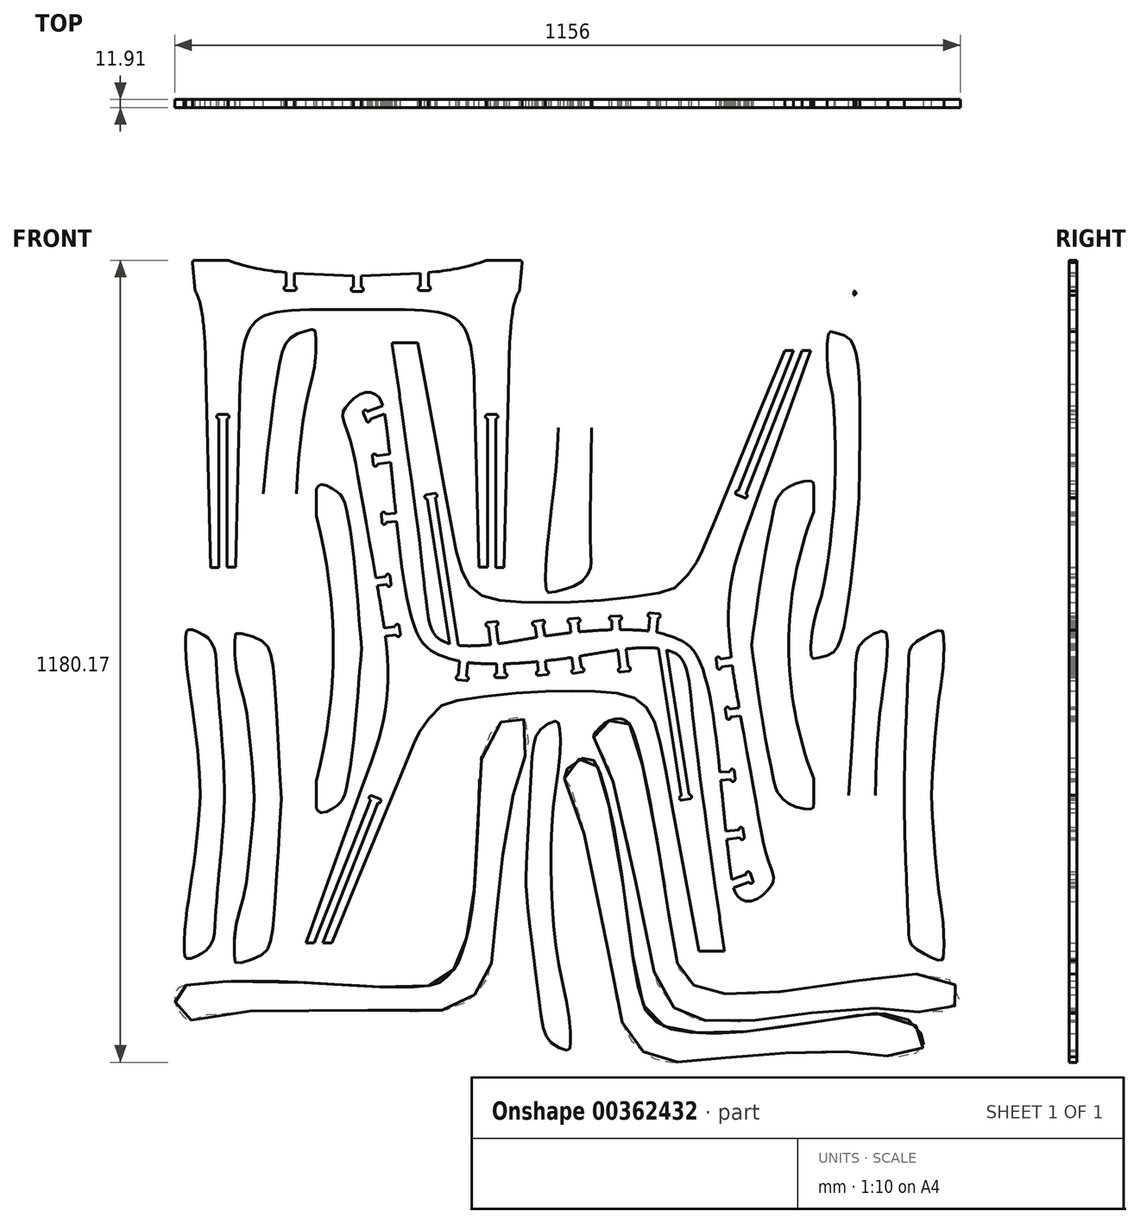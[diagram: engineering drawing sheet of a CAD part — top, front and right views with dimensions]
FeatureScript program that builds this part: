
annotation { "Feature Type Name" : "Feature", "Feature Type Description" : "" }
export const myFeature = defineFeature(function(context is Context, id is Id, definition is map)
    precondition{}
    {
        {
            var Q0;
            Q0=qCreatedBy(makeId("Front.planeOp"),FACE);
            var sketch = newSketch(context, id + "F0", { "sketchPlane" : qUnion([Q0])});
            skLineSegment(sketch, "E0", {"start": v(-81.62, 205.23) * mm, "end": v(-81.62, 184.98) * mm});
            skLineSegment(sketch, "E1", {"start": v(-81.62, 184.98) * mm, "end": v(-81.62, 178.63) * mm});
            skLineSegment(sketch, "E2", {"start": v(-81.62, 178.63) * mm, "end": v(-69.72, 178.63) * mm});
            skLineSegment(sketch, "E3", {"start": v(-69.72, 178.63) * mm, "end": v(-69.72, 204.85) * mm});
            skArc(sketch, "E4", {"start": v(-81.62, 184.98) * mm, "mid": v(-84.8, 181.8) * mm, "end": v(-81.62, 178.63) * mm});
            skArc(sketch, "E5", {"start": v(-69.72, 178.63) * mm, "mid": v(-66.54, 181.8) * mm, "end": v(-69.72, 184.98) * mm});
            skLineSegment(sketch, "E6", {"start": v(17.1, 203.79) * mm, "end": v(17.1, 183.54) * mm});
            skLineSegment(sketch, "E7", {"start": v(17.1, 183.54) * mm, "end": v(17.1, 177.19) * mm});
            skLineSegment(sketch, "E8", {"start": v(17.1, 177.19) * mm, "end": v(23.06, 177.19) * mm});
            skArc(sketch, "E9", {"start": v(17.1, 183.54) * mm, "mid": v(13.93, 180.36) * mm, "end": v(17.1, 177.19) * mm});
            skLineSegment(sketch, "E10", {"start": v(-168.8, -228.88) * mm, "end": v(-168.8, -10.17) * mm});
            skLineSegment(sketch, "E11", {"start": v(-168.8, -10.17) * mm, "end": v(-168.8, -3.82) * mm});
            skLineSegment(sketch, "E12", {"start": v(-168.8, -3.82) * mm, "end": v(-180.71, -3.82) * mm});
            skLineSegment(sketch, "E13", {"start": v(-180.71, -3.82) * mm, "end": v(-180.71, -228.98) * mm});
            skArc(sketch, "E14", {"start": v(-168.8, -10.17) * mm, "mid": v(-165.63, -7) * mm, "end": v(-168.8, -3.82) * mm});
            skArc(sketch, "E15", {"start": v(-180.71, -3.82) * mm, "mid": v(-183.89, -7) * mm, "end": v(-180.71, -10.17) * mm});
            skLineSegment(sketch, "E16", {"start": v(17.1, 199.92) * mm, "end": v(-69.72, 204.07) * mm});
            skLineSegment(sketch, "E17", {"start": v(-155.88, -228.77) * mm, "end": v(-168.8, -228.88) * mm});
            skLineSegment(sketch, "E18", {"start": v(-192.63, -229.08) * mm, "end": v(-201.26, 103.32) * mm});
            skFitSpline(sketch, "E19", {"points": [v(-201.26, 103.32) * mm, v(-215.72, 177.88) * mm, v(-238.76, 190.98) * mm], "startDerivative": vector(-10.73, 144.8) * mm, "endDerivative": vector(-69.3, 19.81) * mm});
            skLineSegment(sketch, "E20", {"start": v(-155.88, -228.77) * mm, "end": v(-149.39, 40.48) * mm});
            skFitSpline(sketch, "E21", {"points": [v(-149.39, 40.48) * mm, v(-131.9, 127.12) * mm, v(31.1, 150.3) * mm], "startDerivative": vector(13.48, 207.58) * mm, "endDerivative": vector(493.77, 1.98) * mm});
            skLineSegment(sketch, "E22", {"start": v(-215.72, 177.88) * mm, "end": v(-219.57, 219.4) * mm});
            skLineSegment(sketch, "E23", {"start": v(-216.4, 222.87) * mm, "end": v(-166.87, 222.87) * mm});
            skPoint(sketch, "E24.visualSharp", {"position": v(-219.89, 222.87) * mm});
            skArc(sketch, "E24.filletArc", {"start": v(-216.4, 222.87) * mm, "mid": v(-218.75, 221.84) * mm, "end": v(-219.57, 219.4) * mm});
            skArc(sketch, "E25", {"start": v(-166.87, 222.87) * mm, "mid": v(-124.87, 211.03) * mm, "end": v(-81.62, 205.23) * mm});
            skLineSegment(sketch, "E26", {"start": v(23.06, 177.19) * mm, "end": v(23.06, 130.99) * mm, "construction": true});
            skPoint(sketch, "E26.endSnap0", {"position": v(23.06, 177.19) * mm});
            skLineSegment(sketch, "E27.trimOffspring", {"start": v(-180.71, -228.98) * mm, "end": v(-192.63, -229.08) * mm});
            skPoint(sketch, "E28.orphan", {"position": v(-168.8, -229.08) * mm});
            skLineSegment(sketch, "E29.MirrorCS", {"start": v(127.74, 184.98) * mm, "end": v(127.74, 178.63) * mm});
            skArc(sketch, "E30.MirrorCS", {"start": v(127.74, 184.98) * mm, "mid": v(130.91, 181.8) * mm, "end": v(127.74, 178.63) * mm});
            skArc(sketch, "E31.MirrorCS", {"start": v(115.83, 178.63) * mm, "mid": v(112.66, 181.8) * mm, "end": v(115.83, 184.98) * mm});
            skLineSegment(sketch, "E32.MirrorCS", {"start": v(127.74, 178.63) * mm, "end": v(115.83, 178.63) * mm});
            skLineSegment(sketch, "E33.MirrorCS", {"start": v(29.01, 183.54) * mm, "end": v(29.01, 177.19) * mm});
            skArc(sketch, "E34.MirrorCS", {"start": v(214.92, -10.17) * mm, "mid": v(211.75, -7) * mm, "end": v(214.92, -3.82) * mm});
            skArc(sketch, "E35.MirrorCS", {"start": v(29.01, 183.54) * mm, "mid": v(32.19, 180.36) * mm, "end": v(29.01, 177.19) * mm});
            skLineSegment(sketch, "E36.MirrorCS", {"start": v(214.92, -10.17) * mm, "end": v(214.92, -3.82) * mm});
            skLineSegment(sketch, "E37.MirrorCS", {"start": v(214.92, -3.82) * mm, "end": v(226.83, -3.82) * mm});
            skArc(sketch, "E38.MirrorCS", {"start": v(226.83, -3.82) * mm, "mid": v(230, -7) * mm, "end": v(226.83, -10.17) * mm});
            skLineSegment(sketch, "E39.MirrorCS", {"start": v(29.01, 177.19) * mm, "end": v(23.06, 177.19) * mm});
            skArc(sketch, "E40.MirrorCS", {"start": v(262.52, 222.87) * mm, "mid": v(264.87, 221.84) * mm, "end": v(265.68, 219.4) * mm});
            skLineSegment(sketch, "E41.MirrorCS", {"start": v(127.74, 205.23) * mm, "end": v(127.74, 184.98) * mm});
            skLineSegment(sketch, "E42.MirrorCS", {"start": v(202, -228.77) * mm, "end": v(214.92, -228.88) * mm});
            skLineSegment(sketch, "E43.MirrorCS", {"start": v(226.83, -228.98) * mm, "end": v(238.74, -229.08) * mm});
            skLineSegment(sketch, "E44.MirrorCS", {"start": v(115.83, 178.63) * mm, "end": v(115.83, 204.85) * mm});
            skLineSegment(sketch, "E45.MirrorCS", {"start": v(29.01, 203.79) * mm, "end": v(29.01, 183.54) * mm});
            skLineSegment(sketch, "E46.MirrorCS", {"start": v(262.52, 222.87) * mm, "end": v(212.98, 222.87) * mm});
            skLineSegment(sketch, "E47.MirrorCS", {"start": v(261.83, 177.88) * mm, "end": v(265.68, 219.4) * mm});
            skLineSegment(sketch, "E48.MirrorCS", {"start": v(226.83, -3.82) * mm, "end": v(226.83, -228.98) * mm});
            skLineSegment(sketch, "E49.MirrorCS", {"start": v(202, -228.77) * mm, "end": v(195.5, 40.48) * mm});
            skLineSegment(sketch, "E50.MirrorCS", {"start": v(214.92, -228.88) * mm, "end": v(214.92, -10.17) * mm});
            skLineSegment(sketch, "E51.MirrorCS", {"start": v(29.01, 199.92) * mm, "end": v(115.83, 204.07) * mm});
            skLineSegment(sketch, "E52.MirrorCS", {"start": v(238.74, -229.08) * mm, "end": v(247.37, 103.32) * mm});
            skPoint(sketch, "E53.MirrorP", {"position": v(214.92, -229.08) * mm});
            skArc(sketch, "E54.MirrorCS", {"start": v(212.98, 222.87) * mm, "mid": v(170.99, 211.03) * mm, "end": v(127.74, 205.23) * mm});
            skPoint(sketch, "E55.MirrorP", {"position": v(266, 222.87) * mm});
            skFitSpline(sketch, "E56.MirrorCS", {"points": [v(247.37, 103.32) * mm, v(261.83, 177.88) * mm, v(284.88, 190.98) * mm], "startDerivative": vector(10.73, 144.8) * mm, "endDerivative": vector(69.3, 19.81) * mm});
            skFitSpline(sketch, "E57.MirrorCS", {"points": [v(195.5, 40.48) * mm, v(178.02, 127.12) * mm, v(15.01, 150.3) * mm], "startDerivative": vector(-13.48, 207.58) * mm, "endDerivative": vector(-493.77, 1.98) * mm});
            skLineSegment(sketch, "E58.MirrorCS", {"start": v(753.94, 177.92) * mm, "end": v(753.94, 171.57) * mm});
            skArc(sketch, "E59.MirrorCS", {"start": v(753.94, 177.92) * mm, "mid": v(757.11, 174.74) * mm, "end": v(753.94, 171.57) * mm});
            skArc(sketch, "E60.MirrorCS", {"start": v(742.03, 171.57) * mm, "mid": v(738.86, 174.74) * mm, "end": v(742.03, 177.92) * mm});
            skLineSegment(sketch, "E61.MirrorCS", {"start": v(753.94, 171.57) * mm, "end": v(742.03, 171.57) * mm});
            skLineSegment(sketch, "E62.MirrorCS", {"start": v(753.96, 198.73) * mm, "end": v(753.94, 177.92) * mm});
            skLineSegment(sketch, "E63.MirrorCS", {"start": v(742.03, 171.57) * mm, "end": v(742.03, 197.79) * mm});
            skArc(sketch, "E64.MirrorCS", {"start": v(655.33, 171.9) * mm, "mid": v(658.5, 168.73) * mm, "end": v(655.33, 165.56) * mm});
            skLineSegment(sketch, "E65.MirrorCS", {"start": v(655.33, 165.56) * mm, "end": v(649.38, 165.56) * mm});
            skLineSegment(sketch, "E66.MirrorCS", {"start": v(655.33, 187.73) * mm, "end": v(655.33, 171.9) * mm});
            skLineSegment(sketch, "E67.MirrorCS", {"start": v(852.75, -1.44) * mm, "end": v(852.84, -7.8) * mm});
            skArc(sketch, "E68.MirrorCS", {"start": v(852.75, -1.44) * mm, "mid": v(855.98, -4.57) * mm, "end": v(852.84, -7.8) * mm});
            skArc(sketch, "E69.MirrorCS", {"start": v(840.94, -7.8) * mm, "mid": v(837.77, -4.62) * mm, "end": v(840.94, -1.44) * mm});
            skLineSegment(sketch, "E70.MirrorCS", {"start": v(852.84, -7.8) * mm, "end": v(840.94, -7.8) * mm});
            skLineSegment(sketch, "E71.MirrorCS", {"start": v(852.75, 224.17) * mm, "end": v(852.75, -1.44) * mm});
            skLineSegment(sketch, "E72.MirrorCS", {"start": v(840.94, -7.8) * mm, "end": v(840.77, 223.4) * mm});
            skLineSegment(sketch, "E73", {"start": v(852.75, 222.83) * mm, "end": v(887.99, 222.83) * mm});
            skFitSpline(sketch, "E74", {"points": [v(891.03, 222.83) * mm, v(891.03, 189.83) * mm, v(886.59, 177.47) * mm, v(876.94, 160.3) * mm, v(874.23, 120.14) * mm, v(863.99, -235.96) * mm], "startDerivative": vector(11.4, -254.33) * mm, "endDerivative": vector(-32.25, -916.44) * mm});
            skLineSegment(sketch, "E75", {"start": v(863.99, -235.96) * mm, "end": v(830.01, -235.96) * mm});
            skFitSpline(sketch, "E76", {"points": [v(830.01, -235.96) * mm, v(821.52, 76.75) * mm, v(816.89, 110.72) * mm, v(795.86, 139.54) * mm, v(769.56, 147.33) * mm, v(688, 142.36) * mm, v(646.79, 141.27) * mm], "startDerivative": vector(-31.45, 1118.64) * mm, "endDerivative": vector(-277.7, 0.32) * mm});
            skLineSegment(sketch, "E77", {"start": v(649.38, 165.56) * mm, "end": v(649.38, 78.6) * mm, "construction": true});
            skArc(sketch, "E78.trimOffspring", {"start": v(655.33, 187.73) * mm, "mid": v(749.53, 197) * mm, "end": v(840.77, 222.2) * mm});
            skLineSegment(sketch, "E79.MirrorCS", {"start": v(446, -1.44) * mm, "end": v(445.9, -7.8) * mm});
            skLineSegment(sketch, "E80.MirrorCS", {"start": v(445.9, -7.8) * mm, "end": v(457.81, -7.8) * mm});
            skLineSegment(sketch, "E81.MirrorCS", {"start": v(544.81, 177.92) * mm, "end": v(544.81, 171.57) * mm});
            skArc(sketch, "E82.MirrorCS", {"start": v(446, -1.44) * mm, "mid": v(442.77, -4.57) * mm, "end": v(445.9, -7.8) * mm});
            skLineSegment(sketch, "E83.MirrorCS", {"start": v(643.42, 165.56) * mm, "end": v(649.38, 165.56) * mm});
            skLineSegment(sketch, "E84.MirrorCS", {"start": v(544.81, 171.57) * mm, "end": v(556.72, 171.57) * mm});
            skArc(sketch, "E85.MirrorCS", {"start": v(556.72, 171.57) * mm, "mid": v(559.9, 174.74) * mm, "end": v(556.72, 177.92) * mm});
            skArc(sketch, "E86.MirrorCS", {"start": v(544.81, 177.92) * mm, "mid": v(541.64, 174.74) * mm, "end": v(544.81, 171.57) * mm});
            skArc(sketch, "E87.MirrorCS", {"start": v(643.42, 171.9) * mm, "mid": v(640.25, 168.73) * mm, "end": v(643.42, 165.56) * mm});
            skArc(sketch, "E88.MirrorCS", {"start": v(457.81, -7.8) * mm, "mid": v(460.98, -4.62) * mm, "end": v(457.8, -1.44) * mm});
            skLineSegment(sketch, "E89.MirrorCS", {"start": v(643.42, 187.73) * mm, "end": v(643.42, 171.9) * mm});
            skLineSegment(sketch, "E90.MirrorCS", {"start": v(556.72, 171.57) * mm, "end": v(556.72, 197.79) * mm});
            skLineSegment(sketch, "E91.MirrorCS", {"start": v(544.8, 198.73) * mm, "end": v(544.81, 177.92) * mm});
            skLineSegment(sketch, "E92.MirrorCS", {"start": v(446, 222.83) * mm, "end": v(410.76, 222.83) * mm});
            skLineSegment(sketch, "E93.MirrorCS", {"start": v(457.81, -7.8) * mm, "end": v(457.98, 223.4) * mm});
            skLineSegment(sketch, "E94.MirrorCS", {"start": v(434.77, -235.96) * mm, "end": v(468.74, -235.96) * mm});
            skLineSegment(sketch, "E95.MirrorCS", {"start": v(446, 224.17) * mm, "end": v(446, -1.44) * mm});
            skFitSpline(sketch, "E96.MirrorCS", {"points": [v(407.72, 222.83) * mm, v(407.72, 189.83) * mm, v(412.16, 177.47) * mm, v(421.82, 160.3) * mm, v(424.52, 120.14) * mm, v(434.77, -235.96) * mm], "startDerivative": vector(-11.4, -254.33) * mm, "endDerivative": vector(32.25, -916.44) * mm});
            skArc(sketch, "E97.MirrorCS", {"start": v(643.42, 187.73) * mm, "mid": v(549.22, 197) * mm, "end": v(457.98, 222.2) * mm});
            skFitSpline(sketch, "E98.MirrorCS", {"points": [v(468.74, -235.96) * mm, v(477.23, 76.75) * mm, v(481.86, 110.72) * mm, v(502.9, 139.54) * mm, v(529.19, 147.33) * mm, v(610.74, 142.36) * mm, v(651.96, 141.27) * mm], "startDerivative": vector(31.45, 1118.64) * mm, "endDerivative": vector(277.7, 0.32) * mm});
            skArc(sketch, "E99.filletArc", {"start": v(891.16, 219.8) * mm, "mid": v(890.18, 221.95) * mm, "end": v(887.99, 222.83) * mm});
            skArc(sketch, "E100.filletArc", {"start": v(410.76, 222.83) * mm, "mid": v(408.57, 221.95) * mm, "end": v(407.59, 219.8) * mm});
            skSolve(sketch);
        }
        {
            var Q0;
            Q0=makeQuery(id+"F0.imprint","IMPRINT",FACE,{"disambiguationData":[TD([[makeQuery(id+"F0.imprint","IMPRINT",EDGE,{"derivedFrom":sQuery(id+"F0.wireOp",EDGE,"E0")}),-1.0]])]});
            var Q1;
            {var subQ15=sQuery(id+"F0.wireOp",EDGE,"E59.MirrorCS");Q1=makeQuery(id+"F0.imprint","IMPRINT",FACE,{"disambiguationData":[TD([[makeQuery(id+"F0.imprint","IMPRINT",EDGE,{"derivedFrom":subQ15}),1.0]])]});}
            extrude(context, id + "F1", {"entities" : qUnion([Q0, Q1]), "depth" : 11.9 * mm});
        }
        {
            var Q0;
            Q0=qCreatedBy(makeId("Front.planeOp"),FACE);
            var sketch = newSketch(context, id + "F2", { "sketchPlane" : qUnion([Q0])});
            skFitSpline(sketch, "E101", {"points": [v(563.44, -793.45) * mm, v(519.52, -470.42) * mm, v(509.79, -388.5) * mm, v(500.05, -362.97) * mm, v(477.12, -349.87) * mm, v(420.34, -348.77) * mm, v(343.35, -360.79) * mm, v(245.08, -370.61) * mm, v(177.93, -367.88) * mm, v(152.22, -360.83) * mm, v(117.78, -337.42) * mm, v(80.17, -153.65) * mm, v(62.72, 0) * mm, v(57.13, 17.73) * mm, v(50.57, 25.07) * mm, v(38.21, 28.93) * mm, v(18.91, 20.43) * mm, v(5.4, 5.76) * mm, v(1.34, -4.19) * mm, v(10.8, -35.07) * mm, v(26.43, -109.3) * mm, v(54.72, -268.66) * mm, v(68.04, -372.42) * mm, v(62.68, -449.28) * mm, v(30.3, -551.87) * mm, v(-52.69, -781.92) * mm], "startDerivative": vector(-604.64, 4230.04) * mm, "endDerivative": vector(-660.59, -1832.87) * mm});
            skLineSegment(sketch, "E102", {"start": v(-52.69, -781.92) * mm, "end": v(-14.57, -781.92) * mm});
            skFitSpline(sketch, "E103", {"points": [v(-14.57, -781.92) * mm, v(109.44, -481.2) * mm, v(115.86, -468.81) * mm, v(140.2, -438.05) * mm, v(170.04, -424.74) * mm, v(275.63, -412.8) * mm, v(358.27, -410.97) * mm, v(415.66, -416.02) * mm, v(444.12, -430.25) * mm, v(461.1, -458.25) * mm, v(478.55, -536.3) * mm, v(525.85, -793.45) * mm], "startDerivative": vector(897.2, 2187.26) * mm, "endDerivative": vector(323.2, -1749.02) * mm});
            skLineSegment(sketch, "E104", {"start": v(525.85, -793.45) * mm, "end": v(563.44, -793.45) * mm});
            skLineSegment(sketch, "E105", {"start": v(-40.26, -781.92) * mm, "end": v(42.52, -570.96) * mm});
            skLineSegment(sketch, "E106", {"start": v(42.52, -570.96) * mm, "end": v(44.84, -565.05) * mm});
            skLineSegment(sketch, "E107", {"start": v(44.84, -565.05) * mm, "end": v(55.92, -569.4) * mm});
            skLineSegment(sketch, "E108", {"start": v(55.92, -569.4) * mm, "end": v(53.6, -575.31) * mm});
            skLineSegment(sketch, "E109", {"start": v(53.6, -575.31) * mm, "end": v(-27.47, -781.92) * mm});
            skArc(sketch, "E110", {"start": v(44.84, -565.05) * mm, "mid": v(40.72, -566.85) * mm, "end": v(42.52, -570.96) * mm});
            skArc(sketch, "E111", {"start": v(53.6, -575.31) * mm, "mid": v(57.72, -573.52) * mm, "end": v(55.92, -569.4) * mm});
            skLineSegment(sketch, "E112", {"start": v(477.02, -339.33) * mm, "end": v(511.6, -563.3) * mm});
            skLineSegment(sketch, "E113", {"start": v(511.6, -563.3) * mm, "end": v(512.56, -569.58) * mm});
            skLineSegment(sketch, "E114", {"start": v(512.56, -569.58) * mm, "end": v(500.8, -571.4) * mm});
            skLineSegment(sketch, "E115", {"start": v(500.8, -571.4) * mm, "end": v(499.82, -565.12) * mm});
            skLineSegment(sketch, "E116", {"start": v(499.82, -565.12) * mm, "end": v(465.97, -345.77) * mm});
            skArc(sketch, "E117", {"start": v(512.56, -569.58) * mm, "mid": v(515.21, -565.95) * mm, "end": v(511.6, -563.3) * mm});
            skArc(sketch, "E118", {"start": v(499.82, -565.12) * mm, "mid": v(497.17, -568.74) * mm, "end": v(500.8, -571.4) * mm});
            skLineSegment(sketch, "E119", {"start": v(405.78, -342.97) * mm, "end": v(410.03, -376.75) * mm});
            skLineSegment(sketch, "E120", {"start": v(410.03, -376.75) * mm, "end": v(410.82, -383.05) * mm});
            skLineSegment(sketch, "E121", {"start": v(410.82, -383.05) * mm, "end": v(422.63, -381.57) * mm});
            skLineSegment(sketch, "E122", {"start": v(422.63, -381.57) * mm, "end": v(421.84, -375.27) * mm});
            skLineSegment(sketch, "E123", {"start": v(421.84, -375.27) * mm, "end": v(417.77, -342.88) * mm});
            skArc(sketch, "E124", {"start": v(410.03, -376.75) * mm, "mid": v(407.27, -380.3) * mm, "end": v(410.82, -383.05) * mm});
            skArc(sketch, "E125", {"start": v(422.63, -381.57) * mm, "mid": v(425.39, -378.02) * mm, "end": v(421.84, -375.27) * mm});
            skLineSegment(sketch, "E126", {"start": v(335.63, -345.28) * mm, "end": v(341.43, -378.83) * mm});
            skLineSegment(sketch, "E127", {"start": v(341.43, -378.83) * mm, "end": v(342.52, -385.09) * mm});
            skLineSegment(sketch, "E128", {"start": v(342.52, -385.09) * mm, "end": v(354.25, -383.06) * mm});
            skLineSegment(sketch, "E129", {"start": v(354.25, -383.06) * mm, "end": v(353.17, -376.8) * mm});
            skLineSegment(sketch, "E130", {"start": v(353.17, -376.8) * mm, "end": v(347.6, -344.63) * mm});
            skArc(sketch, "E131", {"start": v(341.43, -378.83) * mm, "mid": v(338.85, -382.5) * mm, "end": v(342.52, -385.09) * mm});
            skArc(sketch, "E132", {"start": v(354.25, -383.06) * mm, "mid": v(356.84, -379.39) * mm, "end": v(353.17, -376.8) * mm});
            skLineSegment(sketch, "E133", {"start": v(286.66, -347.67) * mm, "end": v(289.48, -381.6) * mm});
            skLineSegment(sketch, "E134", {"start": v(289.48, -381.6) * mm, "end": v(290, -387.93) * mm});
            skLineSegment(sketch, "E135", {"start": v(290, -387.93) * mm, "end": v(301.87, -386.95) * mm});
            skLineSegment(sketch, "E136", {"start": v(301.87, -386.95) * mm, "end": v(301.34, -380.62) * mm});
            skLineSegment(sketch, "E137", {"start": v(301.34, -380.62) * mm, "end": v(298.64, -348.08) * mm});
            skArc(sketch, "E138", {"start": v(289.48, -381.6) * mm, "mid": v(286.58, -385.03) * mm, "end": v(290, -387.93) * mm});
            skArc(sketch, "E139", {"start": v(301.87, -386.95) * mm, "mid": v(304.77, -383.52) * mm, "end": v(301.34, -380.62) * mm});
            skLineSegment(sketch, "E140", {"start": v(227.29, -350.92) * mm, "end": v(228.36, -384.95) * mm});
            skLineSegment(sketch, "E141", {"start": v(228.36, -384.95) * mm, "end": v(228.55, -391.3) * mm});
            skLineSegment(sketch, "E142", {"start": v(228.55, -391.3) * mm, "end": v(240.46, -390.92) * mm});
            skLineSegment(sketch, "E143", {"start": v(240.46, -390.92) * mm, "end": v(240.26, -384.57) * mm});
            skLineSegment(sketch, "E144", {"start": v(240.26, -384.57) * mm, "end": v(239.23, -351.94) * mm});
            skArc(sketch, "E145", {"start": v(228.36, -384.95) * mm, "mid": v(225.28, -388.22) * mm, "end": v(228.55, -391.3) * mm});
            skArc(sketch, "E146", {"start": v(240.46, -390.92) * mm, "mid": v(243.53, -387.65) * mm, "end": v(240.26, -384.57) * mm});
            skLineSegment(sketch, "E147", {"start": v(175.13, -354.26) * mm, "end": v(171.96, -388.16) * mm});
            skLineSegment(sketch, "E148", {"start": v(171.96, -388.16) * mm, "end": v(171.37, -394.48) * mm});
            skLineSegment(sketch, "E149", {"start": v(171.37, -394.48) * mm, "end": v(183.22, -395.59) * mm});
            skLineSegment(sketch, "E150", {"start": v(183.22, -395.59) * mm, "end": v(183.81, -389.27) * mm});
            skLineSegment(sketch, "E151", {"start": v(183.81, -389.27) * mm, "end": v(186.85, -356.76) * mm});
            skArc(sketch, "E152", {"start": v(171.96, -388.16) * mm, "mid": v(168.5, -391.02) * mm, "end": v(171.37, -394.48) * mm});
            skArc(sketch, "E153", {"start": v(183.22, -395.59) * mm, "mid": v(186.68, -392.72) * mm, "end": v(183.81, -389.27) * mm});
            skLineSegment(sketch, "E154", {"start": v(98.9, -147.93) * mm, "end": v(64.94, -150.46) * mm});
            skLineSegment(sketch, "E155", {"start": v(64.94, -150.46) * mm, "end": v(58.61, -150.93) * mm});
            skLineSegment(sketch, "E156", {"start": v(58.61, -150.93) * mm, "end": v(59.5, -162.8) * mm});
            skLineSegment(sketch, "E157", {"start": v(59.5, -162.8) * mm, "end": v(65.83, -162.33) * mm});
            skLineSegment(sketch, "E158", {"start": v(65.83, -162.33) * mm, "end": v(98.39, -159.9) * mm});
            skArc(sketch, "E159", {"start": v(64.94, -150.46) * mm, "mid": v(61.54, -147.53) * mm, "end": v(58.61, -150.93) * mm});
            skArc(sketch, "E160", {"start": v(59.5, -162.8) * mm, "mid": v(62.9, -165.73) * mm, "end": v(65.83, -162.33) * mm});
            skLineSegment(sketch, "E161", {"start": v(85.2, -60.5) * mm, "end": v(51.41, -64.75) * mm});
            skLineSegment(sketch, "E162", {"start": v(51.41, -64.75) * mm, "end": v(45.11, -65.54) * mm});
            skLineSegment(sketch, "E163", {"start": v(45.11, -65.54) * mm, "end": v(46.6, -77.35) * mm});
            skLineSegment(sketch, "E164", {"start": v(46.6, -77.35) * mm, "end": v(52.9, -76.56) * mm});
            skLineSegment(sketch, "E165", {"start": v(52.9, -76.56) * mm, "end": v(85.3, -72.49) * mm});
            skArc(sketch, "E166", {"start": v(51.41, -64.75) * mm, "mid": v(47.87, -62) * mm, "end": v(45.11, -65.54) * mm});
            skArc(sketch, "E167", {"start": v(46.6, -77.35) * mm, "mid": v(50.14, -80.1) * mm, "end": v(52.9, -76.56) * mm});
            skLineSegment(sketch, "E168", {"start": v(70.16, 11.98) * mm, "end": v(38.1, 0.51) * mm});
            skLineSegment(sketch, "E169", {"start": v(38.1, 0.51) * mm, "end": v(32.13, -1.63) * mm});
            skLineSegment(sketch, "E170", {"start": v(32.13, -1.63) * mm, "end": v(36.14, -12.84) * mm});
            skLineSegment(sketch, "E171", {"start": v(36.14, -12.84) * mm, "end": v(42.12, -10.7) * mm});
            skLineSegment(sketch, "E172", {"start": v(42.12, -10.7) * mm, "end": v(92.79, 7.44) * mm});
            skArc(sketch, "E173", {"start": v(38.1, 0.51) * mm, "mid": v(34.05, 2.43) * mm, "end": v(32.13, -1.63) * mm});
            skArc(sketch, "E174", {"start": v(36.14, -12.84) * mm, "mid": v(40.2, -14.76) * mm, "end": v(42.12, -10.7) * mm});
            skPoint(sketch, "E175", {"position": v(67.45, -1.63) * mm});
            skLineSegment(sketch, "E176", {"start": v(32.72, -258.49) * mm, "end": v(66.5, -254.24) * mm});
            skLineSegment(sketch, "E177", {"start": v(66.5, -254.24) * mm, "end": v(72.8, -253.45) * mm});
            skLineSegment(sketch, "E178", {"start": v(72.8, -253.45) * mm, "end": v(71.31, -241.64) * mm});
            skLineSegment(sketch, "E179", {"start": v(71.31, -241.64) * mm, "end": v(65.01, -242.43) * mm});
            skLineSegment(sketch, "E180", {"start": v(65.01, -242.43) * mm, "end": v(32.62, -246.5) * mm});
            skArc(sketch, "E181", {"start": v(66.5, -254.24) * mm, "mid": v(70.04, -257) * mm, "end": v(72.8, -253.45) * mm});
            skArc(sketch, "E182", {"start": v(71.31, -241.64) * mm, "mid": v(67.76, -238.88) * mm, "end": v(65.01, -242.43) * mm});
            skLineSegment(sketch, "E183", {"start": v(46.4, -332.28) * mm, "end": v(80.19, -328.04) * mm});
            skLineSegment(sketch, "E184", {"start": v(80.19, -328.04) * mm, "end": v(86.49, -327.24) * mm});
            skLineSegment(sketch, "E185", {"start": v(86.49, -327.24) * mm, "end": v(85, -315.43) * mm});
            skLineSegment(sketch, "E186", {"start": v(85, -315.43) * mm, "end": v(78.7, -316.22) * mm});
            skLineSegment(sketch, "E187", {"start": v(78.7, -316.22) * mm, "end": v(46.3, -320.3) * mm});
            skArc(sketch, "E188", {"start": v(80.19, -328.04) * mm, "mid": v(83.73, -330.79) * mm, "end": v(86.49, -327.24) * mm});
            skArc(sketch, "E189", {"start": v(85, -315.43) * mm, "mid": v(81.46, -312.68) * mm, "end": v(78.7, -316.22) * mm});
            skFitSpline(sketch, "E190", {"points": [v(74.27, 101.86) * mm, v(118.19, -221.17) * mm, v(127.92, -303.09) * mm, v(137.66, -328.62) * mm, v(160.6, -341.72) * mm, v(217.37, -342.81) * mm, v(294.36, -330.8) * mm, v(392.63, -320.97) * mm, v(459.78, -323.7) * mm, v(485.5, -330.75) * mm, v(519.93, -354.17) * mm, v(557.54, -537.94) * mm, v(575, -691.59) * mm, v(580.58, -709.32) * mm, v(587.14, -716.65) * mm, v(599.5, -720.51) * mm, v(618.8, -712.02) * mm, v(632.31, -697.35) * mm, v(636.37, -687.4) * mm, v(626.91, -656.52) * mm, v(611.28, -582.29) * mm, v(582.99, -422.92) * mm, v(569.67, -319.17) * mm, v(575.03, -242.3) * mm, v(607.4, -139.71) * mm, v(690.4, 90.34) * mm], "startDerivative": vector(604.64, -4230.04) * mm, "endDerivative": vector(660.59, 1832.87) * mm});
            skLineSegment(sketch, "E191", {"start": v(690.4, 90.34) * mm, "end": v(652.28, 90.34) * mm});
            skFitSpline(sketch, "E192", {"points": [v(652.28, 90.34) * mm, v(528.27, -210.38) * mm, v(521.85, -222.77) * mm, v(497.51, -253.53) * mm, v(467.67, -266.85) * mm, v(362.08, -278.78) * mm, v(279.44, -280.62) * mm, v(222.05, -275.57) * mm, v(193.6, -261.34) * mm, v(176.6, -233.33) * mm, v(159.16, -155.29) * mm, v(111.86, 101.86) * mm], "startDerivative": vector(-897.2, -2187.26) * mm, "endDerivative": vector(-323.2, 1749.02) * mm});
            skLineSegment(sketch, "E193", {"start": v(111.86, 101.86) * mm, "end": v(74.27, 101.86) * mm});
            skLineSegment(sketch, "E194", {"start": v(677.98, 90.34) * mm, "end": v(595.2, -120.62) * mm});
            skLineSegment(sketch, "E195", {"start": v(595.2, -120.62) * mm, "end": v(592.87, -126.53) * mm});
            skLineSegment(sketch, "E196", {"start": v(592.87, -126.53) * mm, "end": v(581.79, -122.18) * mm});
            skLineSegment(sketch, "E197", {"start": v(581.79, -122.18) * mm, "end": v(584.1, -116.27) * mm});
            skLineSegment(sketch, "E198", {"start": v(584.1, -116.27) * mm, "end": v(665.18, 90.34) * mm});
            skArc(sketch, "E199", {"start": v(592.87, -126.53) * mm, "mid": v(596.99, -124.74) * mm, "end": v(595.2, -120.62) * mm});
            skArc(sketch, "E200", {"start": v(584.1, -116.27) * mm, "mid": v(580, -118.07) * mm, "end": v(581.79, -122.18) * mm});
            skLineSegment(sketch, "E201", {"start": v(160.69, -352.25) * mm, "end": v(126.12, -128.29) * mm});
            skLineSegment(sketch, "E202", {"start": v(126.12, -128.29) * mm, "end": v(125.15, -122) * mm});
            skLineSegment(sketch, "E203", {"start": v(125.15, -122) * mm, "end": v(136.92, -120.2) * mm});
            skLineSegment(sketch, "E204", {"start": v(136.92, -120.2) * mm, "end": v(137.89, -126.47) * mm});
            skLineSegment(sketch, "E205", {"start": v(137.89, -126.47) * mm, "end": v(171.74, -345.82) * mm});
            skArc(sketch, "E206", {"start": v(125.15, -122) * mm, "mid": v(122.5, -125.63) * mm, "end": v(126.12, -128.29) * mm});
            skArc(sketch, "E207", {"start": v(137.89, -126.47) * mm, "mid": v(140.54, -122.85) * mm, "end": v(136.92, -120.2) * mm});
            skLineSegment(sketch, "E208", {"start": v(231.93, -348.61) * mm, "end": v(227.68, -314.83) * mm});
            skLineSegment(sketch, "E209", {"start": v(227.68, -314.83) * mm, "end": v(226.9, -308.53) * mm});
            skLineSegment(sketch, "E210", {"start": v(226.9, -308.53) * mm, "end": v(215.08, -310.02) * mm});
            skLineSegment(sketch, "E211", {"start": v(215.08, -310.02) * mm, "end": v(215.87, -316.32) * mm});
            skLineSegment(sketch, "E212", {"start": v(215.87, -316.32) * mm, "end": v(219.94, -348.71) * mm});
            skArc(sketch, "E213", {"start": v(227.68, -314.83) * mm, "mid": v(230.44, -311.29) * mm, "end": v(226.9, -308.53) * mm});
            skArc(sketch, "E214", {"start": v(215.08, -310.02) * mm, "mid": v(212.32, -313.56) * mm, "end": v(215.87, -316.32) * mm});
            skLineSegment(sketch, "E215", {"start": v(302.08, -346.3) * mm, "end": v(296.28, -312.76) * mm});
            skLineSegment(sketch, "E216", {"start": v(296.28, -312.76) * mm, "end": v(295.2, -306.5) * mm});
            skLineSegment(sketch, "E217", {"start": v(295.2, -306.5) * mm, "end": v(283.46, -308.53) * mm});
            skLineSegment(sketch, "E218", {"start": v(283.46, -308.53) * mm, "end": v(284.54, -314.79) * mm});
            skLineSegment(sketch, "E219", {"start": v(284.54, -314.79) * mm, "end": v(290.11, -346.96) * mm});
            skArc(sketch, "E220", {"start": v(296.28, -312.76) * mm, "mid": v(298.86, -309.09) * mm, "end": v(295.2, -306.5) * mm});
            skArc(sketch, "E221", {"start": v(283.46, -308.53) * mm, "mid": v(280.87, -312.2) * mm, "end": v(284.54, -314.79) * mm});
            skLineSegment(sketch, "E222", {"start": v(351.05, -343.91) * mm, "end": v(348.23, -309.98) * mm});
            skLineSegment(sketch, "E223", {"start": v(348.23, -309.98) * mm, "end": v(347.7, -303.65) * mm});
            skLineSegment(sketch, "E224", {"start": v(347.7, -303.65) * mm, "end": v(335.84, -304.64) * mm});
            skLineSegment(sketch, "E225", {"start": v(335.84, -304.64) * mm, "end": v(336.37, -310.97) * mm});
            skLineSegment(sketch, "E226", {"start": v(336.37, -310.97) * mm, "end": v(339.07, -343.5) * mm});
            skArc(sketch, "E227", {"start": v(348.23, -309.98) * mm, "mid": v(351.13, -306.56) * mm, "end": v(347.7, -303.65) * mm});
            skArc(sketch, "E228", {"start": v(335.84, -304.64) * mm, "mid": v(332.94, -308.07) * mm, "end": v(336.37, -310.97) * mm});
            skLineSegment(sketch, "E229", {"start": v(410.42, -340.67) * mm, "end": v(409.35, -306.64) * mm});
            skLineSegment(sketch, "E230", {"start": v(409.35, -306.64) * mm, "end": v(409.16, -300.3) * mm});
            skLineSegment(sketch, "E231", {"start": v(409.16, -300.3) * mm, "end": v(397.25, -300.66) * mm});
            skLineSegment(sketch, "E232", {"start": v(397.25, -300.66) * mm, "end": v(397.45, -307.01) * mm});
            skLineSegment(sketch, "E233", {"start": v(397.45, -307.01) * mm, "end": v(398.48, -339.64) * mm});
            skArc(sketch, "E234", {"start": v(409.35, -306.64) * mm, "mid": v(412.43, -303.37) * mm, "end": v(409.16, -300.3) * mm});
            skArc(sketch, "E235", {"start": v(397.25, -300.66) * mm, "mid": v(394.18, -303.94) * mm, "end": v(397.45, -307.01) * mm});
            skLineSegment(sketch, "E236", {"start": v(462.58, -337.33) * mm, "end": v(465.75, -303.43) * mm});
            skLineSegment(sketch, "E237", {"start": v(465.75, -303.43) * mm, "end": v(466.34, -297.1) * mm});
            skLineSegment(sketch, "E238", {"start": v(466.34, -297.1) * mm, "end": v(454.49, -296) * mm});
            skLineSegment(sketch, "E239", {"start": v(454.49, -296) * mm, "end": v(453.9, -302.32) * mm});
            skLineSegment(sketch, "E240", {"start": v(453.9, -302.32) * mm, "end": v(450.86, -334.83) * mm});
            skArc(sketch, "E241", {"start": v(465.75, -303.43) * mm, "mid": v(469.2, -300.56) * mm, "end": v(466.34, -297.1) * mm});
            skArc(sketch, "E242", {"start": v(454.49, -296) * mm, "mid": v(451.03, -298.86) * mm, "end": v(453.9, -302.32) * mm});
            skLineSegment(sketch, "E243", {"start": v(538.81, -543.66) * mm, "end": v(572.77, -541.13) * mm});
            skLineSegment(sketch, "E244", {"start": v(572.77, -541.13) * mm, "end": v(579.1, -540.66) * mm});
            skLineSegment(sketch, "E245", {"start": v(579.1, -540.66) * mm, "end": v(578.21, -528.78) * mm});
            skLineSegment(sketch, "E246", {"start": v(578.21, -528.78) * mm, "end": v(571.88, -529.25) * mm});
            skLineSegment(sketch, "E247", {"start": v(571.88, -529.25) * mm, "end": v(539.32, -531.68) * mm});
            skArc(sketch, "E248", {"start": v(572.77, -541.13) * mm, "mid": v(576.17, -544.06) * mm, "end": v(579.1, -540.66) * mm});
            skArc(sketch, "E249", {"start": v(578.21, -528.78) * mm, "mid": v(574.81, -525.85) * mm, "end": v(571.88, -529.25) * mm});
            skLineSegment(sketch, "E250", {"start": v(552.52, -631.09) * mm, "end": v(586.3, -626.84) * mm});
            skLineSegment(sketch, "E251", {"start": v(586.3, -626.84) * mm, "end": v(592.6, -626.05) * mm});
            skLineSegment(sketch, "E252", {"start": v(592.6, -626.05) * mm, "end": v(591.11, -614.23) * mm});
            skLineSegment(sketch, "E253", {"start": v(591.11, -614.23) * mm, "end": v(584.81, -615.03) * mm});
            skLineSegment(sketch, "E254", {"start": v(584.81, -615.03) * mm, "end": v(552.42, -619.1) * mm});
            skArc(sketch, "E255", {"start": v(586.3, -626.84) * mm, "mid": v(589.84, -629.6) * mm, "end": v(592.6, -626.05) * mm});
            skArc(sketch, "E256", {"start": v(591.11, -614.23) * mm, "mid": v(587.57, -611.48) * mm, "end": v(584.81, -615.03) * mm});
            skLineSegment(sketch, "E257", {"start": v(567.55, -703.57) * mm, "end": v(599.6, -692.1) * mm});
            skLineSegment(sketch, "E258", {"start": v(599.6, -692.1) * mm, "end": v(605.58, -689.96) * mm});
            skLineSegment(sketch, "E259", {"start": v(605.58, -689.96) * mm, "end": v(601.57, -678.75) * mm});
            skLineSegment(sketch, "E260", {"start": v(601.57, -678.75) * mm, "end": v(595.6, -680.89) * mm});
            skLineSegment(sketch, "E261", {"start": v(595.6, -680.89) * mm, "end": v(544.92, -699.03) * mm});
            skArc(sketch, "E262", {"start": v(599.6, -692.1) * mm, "mid": v(603.66, -694.02) * mm, "end": v(605.58, -689.96) * mm});
            skArc(sketch, "E263", {"start": v(601.57, -678.75) * mm, "mid": v(597.5, -676.83) * mm, "end": v(595.6, -680.89) * mm});
            skPoint(sketch, "E264", {"position": v(570.26, -689.96) * mm});
            skLineSegment(sketch, "E265", {"start": v(605, -433.1) * mm, "end": v(571.21, -437.34) * mm});
            skLineSegment(sketch, "E266", {"start": v(571.21, -437.34) * mm, "end": v(564.91, -438.14) * mm});
            skLineSegment(sketch, "E267", {"start": v(564.91, -438.14) * mm, "end": v(566.4, -449.95) * mm});
            skLineSegment(sketch, "E268", {"start": v(566.4, -449.95) * mm, "end": v(572.7, -449.16) * mm});
            skLineSegment(sketch, "E269", {"start": v(572.7, -449.16) * mm, "end": v(605.1, -445.08) * mm});
            skArc(sketch, "E270", {"start": v(571.21, -437.34) * mm, "mid": v(567.67, -434.59) * mm, "end": v(564.91, -438.14) * mm});
            skArc(sketch, "E271", {"start": v(566.4, -449.95) * mm, "mid": v(569.95, -452.7) * mm, "end": v(572.7, -449.16) * mm});
            skLineSegment(sketch, "E272", {"start": v(591.3, -359.3) * mm, "end": v(557.52, -363.55) * mm});
            skLineSegment(sketch, "E273", {"start": v(557.52, -363.55) * mm, "end": v(551.22, -364.34) * mm});
            skLineSegment(sketch, "E274", {"start": v(551.22, -364.34) * mm, "end": v(552.7, -376.16) * mm});
            skLineSegment(sketch, "E275", {"start": v(552.7, -376.16) * mm, "end": v(559, -375.36) * mm});
            skLineSegment(sketch, "E276", {"start": v(559, -375.36) * mm, "end": v(591.4, -371.3) * mm});
            skArc(sketch, "E277", {"start": v(557.52, -363.55) * mm, "mid": v(553.98, -360.8) * mm, "end": v(551.22, -364.34) * mm});
            skArc(sketch, "E278", {"start": v(552.7, -376.16) * mm, "mid": v(556.25, -378.91) * mm, "end": v(559, -375.36) * mm});
            skSolve(sketch);
        }
        {
            var Q0;
            {var subQ59=sQuery(id+"F2.wireOp",EDGE,"E192");Q0=makeQuery(id+"F2.imprint","IMPRINT",FACE,{"disambiguationData":[TD([[makeQuery(id+"F2.imprint","IMPRINT",EDGE,{"derivedFrom":subQ59}),1.0]])]});}
            var Q1;
            {var subQ59=sQuery(id+"F2.wireOp",EDGE,"E103");Q1=makeQuery(id+"F2.imprint","IMPRINT",FACE,{"disambiguationData":[TD([[makeQuery(id+"F2.imprint","IMPRINT",EDGE,{"derivedFrom":subQ59}),1.0]])]});}
            extrude(context, id + "F3", {"entities" : qUnion([Q0, Q1]), "depth" : 11.9 * mm});
        }
        {
            var Q0;
            Q0=qCreatedBy(makeId("Front.planeOp"),FACE);
            var sketch = newSketch(context, id + "F4", { "sketchPlane" : qUnion([Q0])});
            skArc(sketch, "E279", {"start": v(694.79, -147) * mm, "mid": v(667.16, -244.97) * mm, "end": v(658.06, -346.37) * mm});
            skFitSpline(sketch, "E280", {"points": [v(694.79, -147) * mm, v(694.79, -107.63) * mm, v(692.27, -102.25) * mm, v(660.13, -108.9) * mm, v(643.6, -124.06) * mm, v(639.24, -132.55) * mm, v(616.75, -248.93) * mm, v(603.32, -346.37) * mm], "startDerivative": vector(3.23, 327.5) * mm, "endDerivative": vector(-45.2, -373.23) * mm});
            skLineSegment(sketch, "E281", {"start": v(658.06, -346.37) * mm, "end": v(588.13, -346.37) * mm, "construction": true});
            skArc(sketch, "E282.MirrorCS", {"start": v(694.79, -539.58) * mm, "mid": v(667.16, -441.6) * mm, "end": v(658.06, -340.21) * mm});
            skFitSpline(sketch, "E283.MirrorCS", {"points": [v(694.79, -539.58) * mm, v(694.79, -578.95) * mm, v(692.27, -584.33) * mm, v(660.13, -577.67) * mm, v(643.6, -562.52) * mm, v(639.24, -554.03) * mm, v(616.75, -437.65) * mm, v(603.32, -340.21) * mm], "startDerivative": vector(3.23, -327.5) * mm, "endDerivative": vector(-45.2, 373.23) * mm});
            skFitSpline(sketch, "E284", {"points": [v(761.85, -132.17) * mm, v(759.53, 74.75) * mm, v(752.58, 100.23) * mm, v(744.09, 110.27) * mm, v(723.64, 117.3) * mm, v(719.16, 118.24) * mm, v(716.68, 114.7) * mm, v(715.18, 66.12) * mm, v(723.22, 19.2) * mm, v(726.5, -82.63) * mm, v(724.98, -142.31) * mm], "startDerivative": vector(17.6, 1138.98) * mm, "endDerivative": vector(-15.62, -440.68) * mm});
            skFitSpline(sketch, "E285.MirrorCS", {"points": [v(762.68, -118.48) * mm, v(737.88, -323.93) * mm, v(728.2, -348.5) * mm, v(718.67, -357.55) * mm, v(697.58, -362.32) * mm, v(693.03, -362.77) * mm, v(690.95, -358.99) * mm, v(694.74, -310.52) * mm, v(707.83, -264.75) * mm, v(722.15, -163.89) * mm, v(727.13, -104.4) * mm], "startDerivative": vector(-106.32, -1134.15) * mm, "endDerivative": vector(32.38, 439.77) * mm});
            skFitSpline(sketch, "E286", {"points": [v(368.05, -23.29) * mm, v(366.76, 168.9) * mm, v(366.76, 181.88) * mm, v(356.37, 200.7) * mm, v(329.1, 214.34) * mm, v(305.4, 219.65) * mm, v(302.12, 217.91) * mm, v(301.35, 168.7) * mm, v(315.88, 31.67) * mm, v(320.47, -90) * mm], "startDerivative": vector(-18.54, 1163.95) * mm, "endDerivative": vector(7.58, -684.17) * mm});
            skLineSegment(sketch, "E287", {"start": v(372.31, -23.29) * mm, "end": v(300.9, -23.29) * mm, "construction": true});
            skFitSpline(sketch, "E288.MirrorCS", {"points": [v(368.05, -23.29) * mm, v(366.76, -215.47) * mm, v(366.76, -228.46) * mm, v(356.37, -247.29) * mm, v(329.1, -260.92) * mm, v(305.4, -266.23) * mm, v(302.12, -264.5) * mm, v(301.35, -215.27) * mm, v(315.88, -78.25) * mm, v(320.47, 43.42) * mm], "startDerivative": vector(-18.54, -1163.95) * mm, "endDerivative": vector(7.58, 684.17) * mm});
            skFitSpline(sketch, "E289", {"points": [v(834.9, -359.79) * mm, v(838.14, -346.15) * mm, v(860.21, -329.92) * mm, v(881.64, -321.48) * mm, v(884.92, -324) * mm, v(886.07, -328.81) * mm, v(885.6, -371.97) * mm, v(878.91, -424.52) * mm, v(871.32, -506.37) * mm, v(868.52, -565.56) * mm], "startDerivative": vector(8.89, 182.28) * mm, "endDerivative": vector(-12.97, -350.26) * mm});
            skFitSpline(sketch, "E290", {"points": [v(834.9, -359.79) * mm, v(829.22, -501.6) * mm, v(827.99, -566.56) * mm], "startDerivative": vector(-11.45, -260.66) * mm, "endDerivative": vector(-1.74, -145.48) * mm});
            skLineSegment(sketch, "E291", {"start": v(868.52, -565.56) * mm, "end": v(812.78, -565.56) * mm, "construction": true});
            skFitSpline(sketch, "E292.MirrorCS", {"points": [v(834.9, -769.3) * mm, v(838.14, -782.93) * mm, v(860.21, -799.16) * mm, v(881.64, -807.6) * mm, v(884.92, -805.09) * mm, v(886.07, -800.27) * mm, v(885.6, -757.11) * mm, v(878.91, -704.56) * mm, v(871.32, -622.71) * mm, v(868.52, -563.52) * mm], "startDerivative": vector(8.89, -182.28) * mm, "endDerivative": vector(-12.97, 350.26) * mm});
            skFitSpline(sketch, "E293.MirrorCS", {"points": [v(834.9, -769.3) * mm, v(829.22, -627.48) * mm, v(827.99, -562.52) * mm], "startDerivative": vector(-11.45, 260.66) * mm, "endDerivative": vector(-1.74, 145.48) * mm});
            skFitSpline(sketch, "E294", {"points": [v(746.58, -565.74) * mm, v(755.48, -410.76) * mm, v(758.07, -356.22) * mm, v(763.3, -342.62) * mm, v(782, -327.52) * mm, v(798.1, -322.6) * mm, v(802.74, -328.34) * mm, v(801.93, -373.1) * mm, v(794.28, -427.16) * mm, v(788.28, -489.95) * mm, v(785.6, -565.74) * mm], "startDerivative": vector(55.98, 898.5) * mm, "endDerivative": vector(-13.94, -585.33) * mm});
            skLineSegment(sketch, "E295", {"start": v(785.6, -565.74) * mm, "end": v(736.48, -565.74) * mm, "construction": true});
            skFitSpline(sketch, "E296.MirrorCS", {"points": [v(746.58, -563.2) * mm, v(755.48, -718.19) * mm, v(758.07, -772.73) * mm, v(763.3, -786.32) * mm, v(782, -801.43) * mm, v(798.1, -806.34) * mm, v(802.74, -800.6) * mm, v(801.93, -755.84) * mm, v(794.28, -701.79) * mm, v(788.28, -639) * mm, v(785.6, -563.2) * mm], "startDerivative": vector(55.98, -898.5) * mm, "endDerivative": vector(-13.94, 585.33) * mm});
            skFitSpline(sketch, "E297.MirrorCS", {"points": [v(-116.39, -128.89) * mm, v(-90.18, 76.69) * mm, v(-81.29, 102.18) * mm, v(-67.84, 113.6) * mm, v(-47.41, 120.6) * mm, v(-40.86, 121.49) * mm, v(-38.8, 117.83) * mm, v(-39.35, 69.37) * mm, v(-49.93, 23.27) * mm, v(-63.52, -71.98) * mm, v(-66.62, -141.93) * mm], "startDerivative": vector(163.97, 1601.06) * mm, "endDerivative": vector(5.4, -289.07) * mm});
            skFitSpline(sketch, "E298.MirrorCS", {"points": [v(-37.24, -153.05) * mm, v(-36.4, -111.75) * mm, v(-29.44, -106.73) * mm, v(-8.2, -116.38) * mm, v(0, -124.5) * mm, v(7.23, -143.8) * mm, v(21.13, -248.42) * mm, v(29.77, -348.42) * mm], "startDerivative": vector(22.6, 714.39) * mm, "endDerivative": vector(45.2, -373.23) * mm});
            skLineSegment(sketch, "E299.MirrorCS", {"start": v(-128.46, -568.4) * mm, "end": v(-85.2, -569.4) * mm, "construction": true});
            skLineSegment(sketch, "E300.MirrorCS", {"start": v(-207.85, -564.28) * mm, "end": v(-161.39, -565.56) * mm, "construction": true});
            skFitSpline(sketch, "E301.MirrorCS", {"points": [v(-88.63, -569.33) * mm, v(-97.24, -418.41) * mm, v(-103.03, -362.05) * mm, v(-111.15, -342.33) * mm, v(-131.6, -330.77) * mm, v(-154.4, -325.6) * mm, v(-156.35, -328.94) * mm, v(-155.92, -373.63) * mm, v(-142.89, -427.16) * mm, v(-134.68, -489.45) * mm, v(-128.46, -568.4) * mm], "startDerivative": vector(-55.98, 898.5) * mm, "endDerivative": vector(13.94, -585.33) * mm});
            skFitSpline(sketch, "E302.MirrorCS", {"points": [v(-185.26, -358.38) * mm, v(-192.57, -337.76) * mm, v(-204.42, -327.86) * mm, v(-220.49, -320.72) * mm, v(-226.65, -321.04) * mm, v(-229.25, -326.4) * mm, v(-227.95, -374.77) * mm, v(-221.57, -422.22) * mm, v(-211.2, -507.79) * mm, v(-207.85, -564.28) * mm], "startDerivative": vector(-8.89, 182.28) * mm, "endDerivative": vector(12.97, -350.26) * mm});
            skFitSpline(sketch, "E303.MirrorCS", {"points": [v(-185.26, -358.38) * mm, v(-174.82, -499.16) * mm, v(-172.37, -565.25) * mm], "startDerivative": vector(11.45, -260.66) * mm, "endDerivative": vector(1.74, -145.48) * mm});
            skArc(sketch, "E304", {"start": v(-12.3, -348.42) * mm, "mid": v(-18.57, -249.94) * mm, "end": v(-37.24, -153.05) * mm});
            skFitSpline(sketch, "E305.MirrorCS", {"points": [v(-88.63, -569.33) * mm, v(-97.7, -718.55) * mm, v(-103.64, -774.9) * mm, v(-111.8, -794.6) * mm, v(-132.28, -806.1) * mm, v(-155.1, -811.2) * mm, v(-157.05, -807.88) * mm, v(-156.5, -763.18) * mm, v(-143.34, -709.68) * mm, v(-134.98, -647.42) * mm, v(-128.46, -568.4) * mm], "startDerivative": vector(-58.2, -898.35) * mm, "endDerivative": vector(15.39, 585.3) * mm});
            skFitSpline(sketch, "E306.MirrorCS", {"points": [v(-187.1, -767.03) * mm, v(-175.57, -626.34) * mm, v(-172.4, -562.54) * mm], "startDerivative": vector(13.48, 260.56) * mm, "endDerivative": vector(2.87, 145.46) * mm});
            skFitSpline(sketch, "E307.MirrorCS", {"points": [v(-187.1, -767.03) * mm, v(-194.57, -787.6) * mm, v(-206.5, -797.4) * mm, v(-222.62, -804.42) * mm, v(-228.79, -804.04) * mm, v(-231.34, -798.67) * mm, v(-229.67, -750.3) * mm, v(-222.92, -702.91) * mm, v(-211.89, -617.43) * mm, v(-207.91, -562.5) * mm], "startDerivative": vector(-10.3, -182.2) * mm, "endDerivative": vector(15.7, 350.14) * mm});
            skLineSegment(sketch, "E308", {"start": v(-118.33, -120.44) * mm, "end": v(-57.04, -120.44) * mm, "construction": true});
            skFitSpline(sketch, "E309.MirrorCS", {"points": [v(-116.39, -112) * mm, v(-90.18, -317.57) * mm, v(-81.29, -343.06) * mm, v(-67.84, -354.48) * mm, v(-47.41, -361.48) * mm, v(-40.86, -362.37) * mm, v(-38.8, -358.7) * mm, v(-39.35, -310.25) * mm, v(-49.93, -264.15) * mm, v(-63.52, -168.9) * mm, v(-66.62, -98.94) * mm], "startDerivative": vector(163.97, -1601.06) * mm, "endDerivative": vector(5.4, 289.07) * mm});
            skLineSegment(sketch, "E310", {"start": v(-12.3, -348.42) * mm, "end": v(36.83, -348.42) * mm, "construction": true});
            skPoint(sketch, "E310.endSnap0", {"position": v(-12.3, -348.42) * mm});
            skPoint(sketch, "E311.orphan", {"position": v(-37.24, -543.8) * mm});
            skFitSpline(sketch, "E312.MirrorCS", {"points": [v(-37.24, -543.8) * mm, v(-36.4, -585.1) * mm, v(-29.44, -590.11) * mm, v(-8.2, -580.46) * mm, v(0, -572.35) * mm, v(7.23, -553.05) * mm, v(21.13, -448.42) * mm, v(29.77, -348.42) * mm], "startDerivative": vector(22.6, -714.39) * mm, "endDerivative": vector(45.2, 373.23) * mm});
            skArc(sketch, "E313.MirrorCS", {"start": v(-12.3, -348.42) * mm, "mid": v(-18.57, -446.9) * mm, "end": v(-37.24, -543.8) * mm});
            skSolve(sketch);
        }
        {
            var Q0;
            {var subQ5=sQuery(id+"F4.wireOp",EDGE,"E306.MirrorCS");Q0=makeQuery(id+"F4.imprint","IMPRINT",FACE,{"disambiguationData":[TD([[makeQuery(id+"F4.imprint","IMPRINT",EDGE,{"derivedFrom":subQ5}),1.0]])]});}
            var Q1;
            Q1=makeQuery(id+"F4.imprint","IMPRINT",FACE,{"disambiguationData":[TD([[makeQuery(id+"F4.imprint","IMPRINT",EDGE,{"derivedFrom":sQuery(id+"F4.wireOp",EDGE,"E301.MirrorCS")}),1.0]])]});
            var Q2;
            {var subQ0=sQuery(id+"F4.wireOp",EDGE,"E309.MirrorCS");var subQ1=sQuery(id+"F4.wireOp",EDGE,"E297.MirrorCS");var subQ2=makeQuery(id+"F4.imprint","INTERSECT",VERTEX,{"disambiguationData":[OD(0.0)],"derivedFrom":[subQ1,subQ0]});Q2=makeQuery(id+"F4.imprint","IMPRINT",FACE,{"disambiguationData":[TD([[makeQuery(id+"F4.imprint","IMPRINT",EDGE,{"disambiguationData":[TD([[subQ2,-1.0]])],"derivedFrom":subQ1}),-1.0]])]});}
            var Q3;
            Q3=makeQuery(id+"F4.imprint","IMPRINT",FACE,{"disambiguationData":[TD([[makeQuery(id+"F4.imprint","IMPRINT",EDGE,{"derivedFrom":sQuery(id+"F4.wireOp",EDGE,"E298.MirrorCS")}),-1.0]])]});
            var Q4;
            Q4=makeQuery(id+"F4.imprint","IMPRINT",FACE,{"disambiguationData":[TD([[makeQuery(id+"F4.imprint","IMPRINT",EDGE,{"derivedFrom":sQuery(id+"F4.wireOp",EDGE,"E286")}),1.0]])]});
            var Q5;
            {var subQ0=sQuery(id+"F4.wireOp",EDGE,"E280");var subQ1=sQuery(id+"F4.wireOp",EDGE,"E279");var subQ2=makeQuery(id+"F4.imprint","INTERSECT",VERTEX,{"derivedFrom":[subQ1,subQ0]});Q5=makeQuery(id+"F4.imprint","IMPRINT",FACE,{"disambiguationData":[TD([[makeQuery(id+"F4.imprint","IMPRINT",EDGE,{"disambiguationData":[TD([[subQ2,-1.0]])],"derivedFrom":subQ1}),-1.0]])]});}
            var Q6;
            Q6=makeQuery(id+"F4.imprint","IMPRINT",FACE,{"disambiguationData":[TD([[makeQuery(id+"F4.imprint","IMPRINT",EDGE,{"derivedFrom":sQuery(id+"F4.wireOp",EDGE,"E284")}),1.0]])]});
            var Q7;
            {var subQ0=sQuery(id+"F4.wireOp",EDGE,"E296.MirrorCS");var subQ1=sQuery(id+"F4.wireOp",EDGE,"E294");var subQ2=makeQuery(id+"F4.imprint","INTERSECT",VERTEX,{"disambiguationData":[OD(0.0)],"derivedFrom":[subQ1,subQ0]});Q7=makeQuery(id+"F4.imprint","IMPRINT",FACE,{"disambiguationData":[TD([[makeQuery(id+"F4.imprint","IMPRINT",EDGE,{"disambiguationData":[TD([[subQ2,-1.0]])],"derivedFrom":subQ1}),-1.0]])]});}
            var Q8;
            {var subQ0=sQuery(id+"F4.wireOp",EDGE,"E290");var subQ1=sQuery(id+"F4.wireOp",EDGE,"E289");var subQ2=makeQuery(id+"F4.imprint","INTERSECT",VERTEX,{"derivedFrom":[subQ1,subQ0]});Q8=makeQuery(id+"F4.imprint","IMPRINT",FACE,{"disambiguationData":[TD([[makeQuery(id+"F4.imprint","IMPRINT",EDGE,{"disambiguationData":[TD([[subQ2,-1.0]])],"derivedFrom":subQ1}),-1.0]])]});}
            extrude(context, id + "F5", {"entities" : qUnion([Q0, Q1, Q2, Q3, Q4, Q5, Q6, Q7, Q8]), "depth" : 11.9 * mm});
        }
        {
            var Q0;
            Q0=qCreatedBy(makeId("Front.planeOp"),FACE);
            var sketch = newSketch(context, id + "F6", { "sketchPlane" : qUnion([Q0])});
            skFitSpline(sketch, "E314", {"points": [v(370.83, -478.96) * mm, v(379.94, -491.3) * mm, v(424.1, -646.9) * mm, v(463.42, -838.42) * mm, v(478.7, -867.9) * mm, v(506.49, -887.76) * mm, v(525.05, -894.86) * mm, v(585.1, -897.32) * mm, v(632.33, -891.86) * mm, v(727.06, -881.2) * mm, v(805.05, -878.24) * mm, v(844.65, -882.95) * mm, v(880.53, -882.95) * mm, v(904.22, -873.21) * mm, v(909.9, -866.23) * mm, v(908.93, -852.92) * mm, v(892.38, -834.9) * mm, v(850.66, -827.11) * mm, v(783.95, -833.6) * mm, v(646.35, -853.08) * mm, v(570.38, -857.3) * mm, v(543.44, -852.43) * mm, v(519.74, -844.97) * mm, v(507, -835.03) * mm, v(498.29, -822.4) * mm, v(488.17, -782.3) * mm, v(476.78, -708.18) * mm, v(450.82, -557.16) * mm, v(432.92, -481.42) * mm, v(422.82, -457.95) * mm, v(416.45, -453.26) * mm, v(408.58, -451.64) * mm, v(390.78, -456.3) * mm, v(376.11, -468.84) * mm, v(370.7, -477.19) * mm, v(370.83, -478.96) * mm]});
            skFitSpline(sketch, "E315", {"points": [v(328.07, -539.5) * mm, v(334.62, -547.83) * mm, v(390.6, -784.86) * mm, v(415.17, -905.52) * mm, v(432.33, -931.67) * mm, v(452.21, -947.5) * mm, v(477.09, -956.71) * mm, v(533.5, -953.71) * mm, v(584.78, -949.17) * mm, v(682.98, -941.54) * mm, v(754.84, -942.1) * mm, v(791.77, -946.33) * mm, v(831.78, -947.87) * mm, v(855.68, -935.72) * mm, v(856.76, -927.65) * mm, v(853.52, -915.96) * mm, v(839.88, -898.1) * mm, v(797.68, -885.44) * mm, v(734.38, -891.94) * mm, v(614.59, -909.46) * mm, v(544.8, -914.97) * mm, v(503.25, -911.98) * mm, v(481.45, -907.4) * mm, v(462.4, -897.06) * mm, v(449.74, -884.91) * mm, v(436.68, -846.1) * mm, v(424.64, -772.03) * mm, v(402.27, -619.66) * mm, v(384.38, -543.93) * mm, v(376.39, -521.2) * mm, v(370.38, -512.2) * mm, v(362.6, -509.33) * mm, v(345.13, -513.16) * mm, v(328.48, -532.13) * mm, v(327.66, -538.4) * mm, v(328.07, -539.5) * mm]});
            skFitSpline(sketch, "E316", {"points": [v(-221.18, -895) * mm, v(-211.76, -890.15) * mm, v(31.6, -880.43) * mm, v(154.73, -879.34) * mm, v(183.68, -867.48) * mm, v(203.01, -850.99) * mm, v(216.8, -828.33) * mm, v(224.62, -772.39) * mm, v(229.95, -721.17) * mm, v(241.2, -623.32) * mm, v(255.46, -552.89) * mm, v(266.65, -517.45) * mm, v(275.8, -478.46) * mm, v(268.43, -452.69) * mm, v(260.72, -450.08) * mm, v(248.63, -451.04) * mm, v(228.5, -461.01) * mm, v(208.02, -500.03) * mm, v(202.3, -563.4) * mm, v(196.65, -684.34) * mm, v(188.74, -753.9) * mm, v(177.89, -794.1) * mm, v(169.22, -814.64) * mm, v(155.44, -831.37) * mm, v(141.1, -841.47) * mm, v(100.51, -846.88) * mm, v(25.5, -844.58) * mm, v(-128.33, -837.46) * mm, v(-206.09, -840.57) * mm, v(-229.91, -844.08) * mm, v(-239.9, -848.25) * mm, v(-244.2, -855.34) * mm, v(-243.78, -873.22) * mm, v(-228.34, -893.19) * mm, v(-222.33, -895.2) * mm, v(-221.18, -895) * mm]});
            skFitSpline(sketch, "E317", {"points": [v(308.78, -698.87) * mm, v(310.96, -589.13) * mm, v(321.88, -497.4) * mm, v(320.25, -463) * mm, v(318.62, -456.5) * mm, v(314.56, -455.16) * mm, v(295.65, -464.8) * mm, v(284.84, -481.02) * mm, v(279.62, -521.2) * mm, v(272.22, -665.64) * mm, v(271.43, -698.08) * mm], "startDerivative": vector(-11.88, 673.43) * mm, "endDerivative": vector(-0.02, -302.85) * mm});
            skLineSegment(sketch, "E318", {"start": v(313.95, -698.08) * mm, "end": v(258, -698.08) * mm, "construction": true});
            skFitSpline(sketch, "E319.MirrorCS", {"points": [v(308.77, -698.08) * mm, v(318.38, -806.25) * mm, v(335.73, -896.98) * mm, v(336.52, -931.41) * mm, v(335.35, -938) * mm, v(331.4, -939.64) * mm, v(311.86, -931.35) * mm, v(299.93, -915.93) * mm, v(291.9, -876.21) * mm, v(274.35, -732.66) * mm, v(271.43, -698.08) * mm], "startDerivative": vector(35.56, -672.6) * mm, "endDerivative": vector(-21.34, 302.1) * mm});
            skSolve(sketch);
        }
        {
            var Q0;
            Q0=makeQuery(id+"F6.imprint","IMPRINT",FACE,{"disambiguationData":[TD([[makeQuery(id+"F6.imprint","IMPRINT",EDGE,{"derivedFrom":sQuery(id+"F6.wireOp",EDGE,"E316")}),1.0]])]});
            var Q1;
            {var subQ0=sQuery(id+"F6.wireOp",EDGE,"E319.MirrorCS");Q1=makeQuery(id+"F6.imprint","IMPRINT",FACE,{"disambiguationData":[TD([[makeQuery(id+"F6.imprint","IMPRINT",EDGE,{"derivedFrom":subQ0}),-1.0]])]});}
            var Q2;
            Q2=makeQuery(id+"F6.imprint","IMPRINT",FACE,{"disambiguationData":[TD([[makeQuery(id+"F6.imprint","IMPRINT",EDGE,{"derivedFrom":sQuery(id+"F6.wireOp",EDGE,"E315")}),1.0]])]});
            var Q3;
            Q3=makeQuery(id+"F6.imprint","IMPRINT",FACE,{"disambiguationData":[TD([[makeQuery(id+"F6.imprint","IMPRINT",EDGE,{"derivedFrom":sQuery(id+"F6.wireOp",EDGE,"E314")}),1.0]])]});
            extrude(context, id + "F7", {"entities" : qUnion([Q0, Q1, Q2, Q3]), "depth" : 11.9 * mm});
        }
    });
